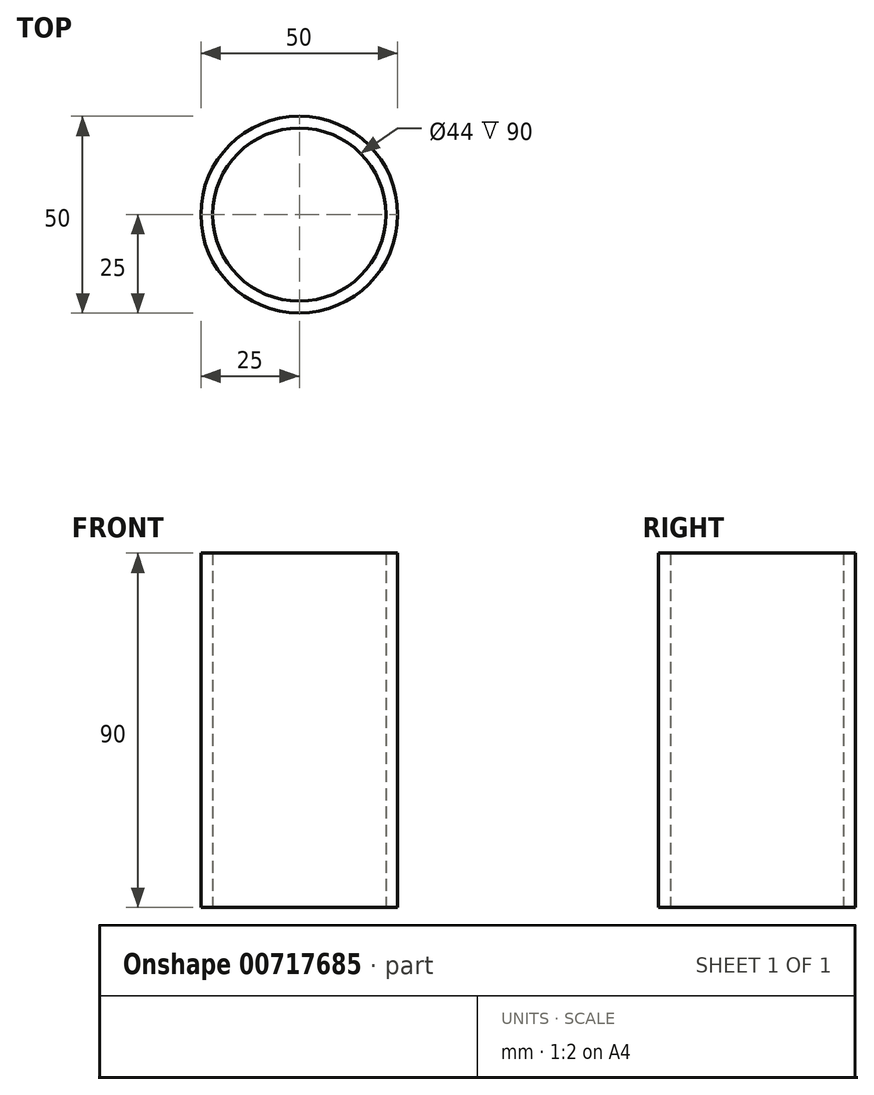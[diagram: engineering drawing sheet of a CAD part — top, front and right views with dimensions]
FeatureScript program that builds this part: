
annotation { "Feature Type Name" : "Feature", "Feature Type Description" : "" }
export const myFeature = defineFeature(function(context is Context, id is Id, definition is map)
    precondition{}
    {
        {
            var Q0;
            Q0=qCreatedBy(makeId("Front.planeOp"),FACE);
            var sketch = newSketch(context, id + "F0", { "sketchPlane" : qUnion([Q0])});
            skLineSegment(sketch, "E0.bottom", {"start": v(-25, 90) * mm, "end": v(-22, 90) * mm});
            skLineSegment(sketch, "E0.top", {"start": v(-25, 0) * mm, "end": v(-22, 0) * mm});
            skLineSegment(sketch, "E0.left", {"start": v(-25, 90) * mm, "end": v(-25, 0) * mm});
            skLineSegment(sketch, "E0.right", {"start": v(-22, 90) * mm, "end": v(-22, 0) * mm});
            skLineSegment(sketch, "E1", {"start": v(0, 0) * mm, "end": v(0, 127.39) * mm, "construction": true});
            skSolve(sketch);
        }
        {
            var Q0;
            Q0=makeQuery(id+"F0.imprint","IMPRINT",FACE,{"disambiguationData":[TD([[makeQuery(id+"F0.imprint","IMPRINT",EDGE,{"derivedFrom":sQuery(id+"F0.wireOp",EDGE,"E0.bottom")}),-1.0]])]});
            var Q1;
            Q1=sQuery(id+"F0.wireOp",EDGE,"E1");
            revolve(context, id + "F1", {"surfaceOperationType" : NewSurfaceOperationType.NEW, "entities" : qUnion([Q0]), "axis" : qUnion([Q1]), "revolveType" : RevolveType.FULL});
        }
    });
